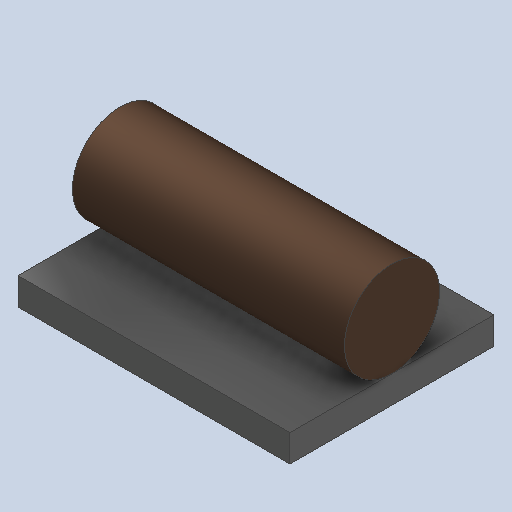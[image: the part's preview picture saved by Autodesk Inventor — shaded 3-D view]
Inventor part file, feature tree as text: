
AUTODESK INVENTOR PART (.ipt)
format: ipt  version: 2025.2 (Build 292293000, 293)  size: 130,560 bytes
history: native  units: mm
features: extrude x2, sketch x2
ambient origin geometry x8: Origin, YZ Plane, XZ Plane, XY Plane, X Axis, Y Axis, Z Axis, Center Point
bodies: Solid1 (feature_tree)
feature tree (4):
  extrude  "Extrusion1"  Depth=15.0mm
  extrude  "Extrusion2"  Depth=2.0mm
  sketch  "Sketch1"  dims[d0=20.0mm d1=15.0mm]
  sketch  "Sketch2"  dims[d2=9.0mm d3=0.0mm d4=2.0mm d5=9.0mm d6=0.0mm]
